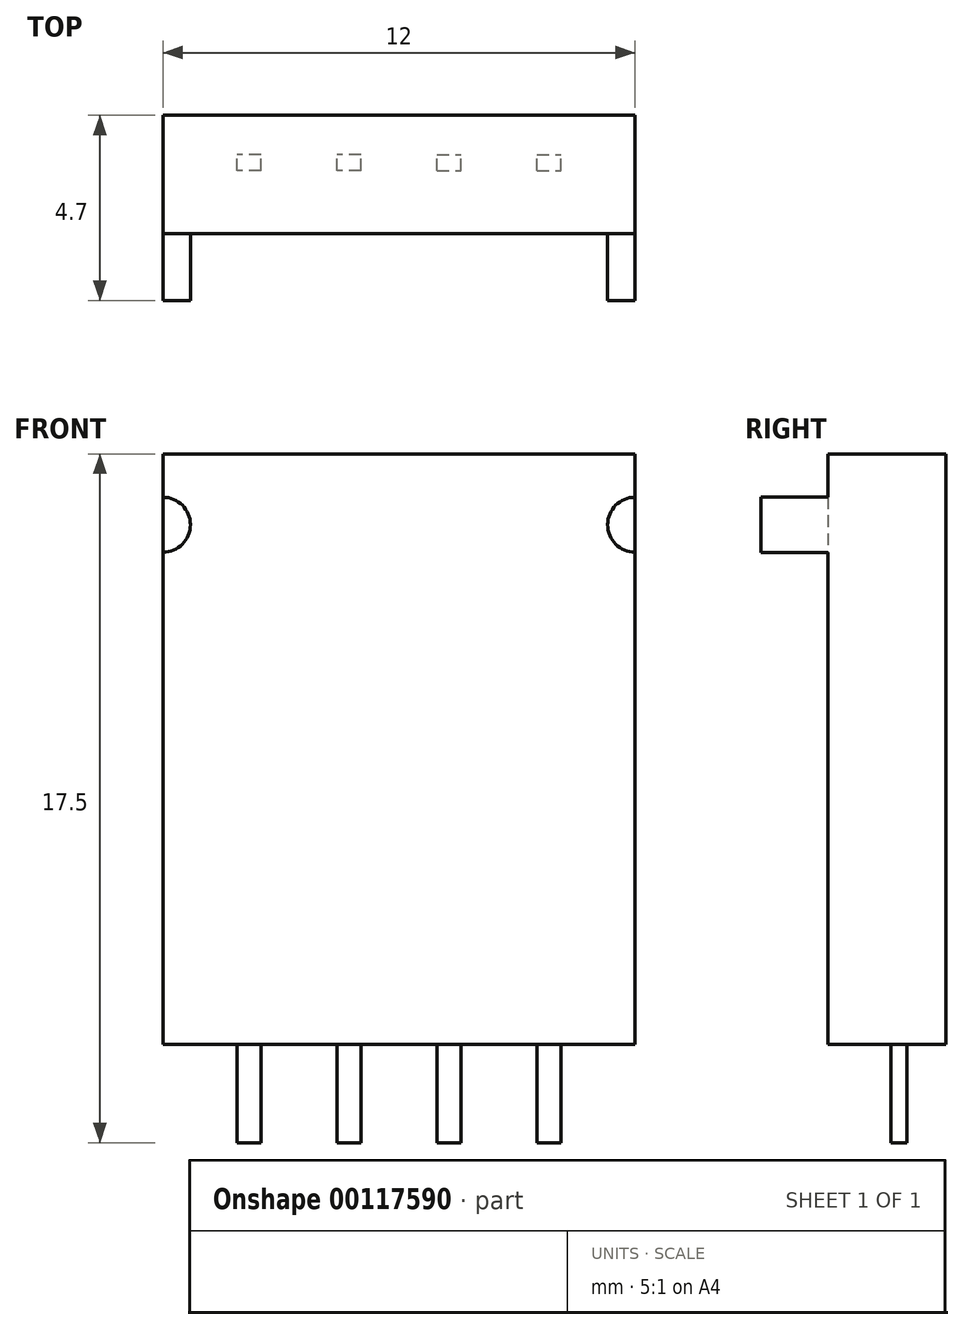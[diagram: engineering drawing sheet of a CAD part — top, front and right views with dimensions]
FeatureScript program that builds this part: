
annotation { "Feature Type Name" : "Feature", "Feature Type Description" : "" }
export const myFeature = defineFeature(function(context is Context, id is Id, definition is map)
    precondition{}
    {
        {
            var Q0;
            Q0=qCreatedBy(makeId("Front.planeOp"),FACE);
            var sketch = newSketch(context, id + "F0", { "sketchPlane" : qUnion([Q0])});
            skLineSegment(sketch, "E0.bottom", {"start": v(-6, 7.5) * mm, "end": v(6, 7.5) * mm});
            skLineSegment(sketch, "E0.top", {"start": v(-6, -7.5) * mm, "end": v(6, -7.5) * mm});
            skLineSegment(sketch, "E0.left", {"start": v(-6, 7.5) * mm, "end": v(-6, -7.5) * mm});
            skLineSegment(sketch, "E0.right", {"start": v(6, 7.5) * mm, "end": v(6, -7.5) * mm});
            skLineSegment(sketch, "E1", {"start": v(0, 7.5) * mm, "end": v(0, -7.5) * mm, "construction": true});
            skLineSegment(sketch, "E2", {"start": v(6, 0) * mm, "end": v(-6, 0) * mm, "construction": true});
            skSolve(sketch);
        }
        {
            var Q0;
            Q0=makeQuery(id+"F0.imprint","IMPRINT",FACE,{"disambiguationData":[TD([[makeQuery(id+"F0.imprint","IMPRINT",EDGE,{"derivedFrom":sQuery(id+"F0.wireOp",EDGE,"E0.bottom")}),-1.0]])]});
            extrude(context, id + "F1", {"entities" : qUnion([Q0]), "endBound" : BoundingType.SYMMETRIC, "depth" : 4.7 * mm});
        }
        {
            var Q0;
            Q0=makeQuery(id+"F1.opExtrude","CAP_FACE",FACE,{"disambiguationData":[OSD([sQuery(id+"F0.wireOp",EDGE,"E0.bottom"),sQuery(id+"F0.wireOp",EDGE,"E0.top"),sQuery(id+"F0.wireOp",EDGE,"E0.left"),sQuery(id+"F0.wireOp",EDGE,"E0.right")])],"isStart":false});
            var sketch = newSketch(context, id + "F2", { "sketchPlane" : qUnion([Q0])});
            skLineSegment(sketch, "E3", {"start": v(-4.2, -3.2) * mm, "end": v(-2.7, -3.2) * mm});
            skLineSegment(sketch, "E4", {"start": v(-4.2, -1.6) * mm, "end": v(-2.7, -1.6) * mm});
            skLineSegment(sketch, "E5", {"start": v(-4.2, -0.8) * mm, "end": v(-2.7, -0.8) * mm});
            skLineSegment(sketch, "E6", {"start": v(-4.2, 1.6) * mm, "end": v(-2.7, 1.6) * mm});
            skLineSegment(sketch, "E7", {"start": v(-4.2, 3.2) * mm, "end": v(-2.7, 3.2) * mm});
            skLineSegment(sketch, "E8", {"start": v(-4.2, 0.8) * mm, "end": v(-2.7, 0.8) * mm});
            skLineSegment(sketch, "E9", {"start": v(-4.2, -3.2) * mm, "end": v(-4.2, -1.6) * mm});
            skLineSegment(sketch, "E10", {"start": v(4.2, -3.2) * mm, "end": v(4.2, -1.6) * mm});
            skLineSegment(sketch, "E11", {"start": v(-2.7, 3.2) * mm, "end": v(-2.7, 1.6) * mm});
            skLineSegment(sketch, "E12", {"start": v(-1.9, 3.2) * mm, "end": v(-1.9, 1.6) * mm});
            skLineSegment(sketch, "E13", {"start": v(-0.4, 3.2) * mm, "end": v(-0.4, 1.6) * mm});
            skLineSegment(sketch, "E14", {"start": v(0.4, 3.2) * mm, "end": v(0.4, 1.6) * mm});
            skLineSegment(sketch, "E15", {"start": v(1.9, 3.2) * mm, "end": v(1.9, 1.6) * mm});
            skLineSegment(sketch, "E16", {"start": v(2.7, 3.2) * mm, "end": v(2.7, 1.6) * mm});
            skArc(sketch, "E17", {"start": v(6, -5) * mm, "mid": v(5.3, -5.7) * mm, "end": v(6, -6.4) * mm});
            skArc(sketch, "E18", {"start": v(-6, -6.4) * mm, "mid": v(-5.3, -5.7) * mm, "end": v(-6, -5) * mm});
            skArc(sketch, "E19", {"start": v(-0.7, 7.5) * mm, "mid": v(0, 6.8) * mm, "end": v(0.7, 7.5) * mm});
            skLineSegment(sketch, "E20", {"start": v(-6, -5.7) * mm, "end": v(6, -5.7) * mm, "construction": true});
            skArc(sketch, "E21.MirrorCS", {"start": v(6, 5) * mm, "mid": v(5.3, 5.7) * mm, "end": v(6, 6.4) * mm});
            skArc(sketch, "E22.MirrorCS", {"start": v(-6, 6.4) * mm, "mid": v(-5.3, 5.7) * mm, "end": v(-6, 5) * mm});
            skLineSegment(sketch, "E23.trimOffspring", {"start": v(-1.9, 3.2) * mm, "end": v(-0.4, 3.2) * mm});
            skLineSegment(sketch, "E24.trimOffspring", {"start": v(-1.9, 1.6) * mm, "end": v(-0.4, 1.6) * mm});
            skLineSegment(sketch, "E25.trimOffspring", {"start": v(-1.9, 0.8) * mm, "end": v(-0.4, 0.8) * mm});
            skLineSegment(sketch, "E26.trimOffspring", {"start": v(-2.7, 0.8) * mm, "end": v(-2.7, -0.8) * mm});
            skLineSegment(sketch, "E27.trimOffspring", {"start": v(-4.2, 1.6) * mm, "end": v(-4.2, 3.2) * mm});
            skLineSegment(sketch, "E28.trimOffspring", {"start": v(-4.2, -0.8) * mm, "end": v(-4.2, 0.8) * mm});
            skLineSegment(sketch, "E29.trimOffspring", {"start": v(-2.7, -1.6) * mm, "end": v(-2.7, -3.2) * mm});
            skLineSegment(sketch, "E30.trimOffspring", {"start": v(-1.9, -1.6) * mm, "end": v(-1.9, -3.2) * mm});
            skLineSegment(sketch, "E31.trimOffspring", {"start": v(-1.9, -0.8) * mm, "end": v(-0.4, -0.8) * mm});
            skLineSegment(sketch, "E32.trimOffspring", {"start": v(-1.9, -1.6) * mm, "end": v(-0.4, -1.6) * mm});
            skLineSegment(sketch, "E33.trimOffspring", {"start": v(-1.9, -3.2) * mm, "end": v(-0.4, -3.2) * mm});
            skLineSegment(sketch, "E34.trimOffspring", {"start": v(0.4, -3.2) * mm, "end": v(1.9, -3.2) * mm});
            skLineSegment(sketch, "E35.trimOffspring", {"start": v(0.4, -1.6) * mm, "end": v(1.9, -1.6) * mm});
            skLineSegment(sketch, "E36.trimOffspring", {"start": v(0.4, -0.8) * mm, "end": v(1.9, -0.8) * mm});
            skLineSegment(sketch, "E37.trimOffspring", {"start": v(0.4, 0.8) * mm, "end": v(1.9, 0.8) * mm});
            skLineSegment(sketch, "E38.trimOffspring", {"start": v(0.4, 1.6) * mm, "end": v(1.9, 1.6) * mm});
            skLineSegment(sketch, "E39.trimOffspring", {"start": v(0.4, 3.2) * mm, "end": v(1.9, 3.2) * mm});
            skLineSegment(sketch, "E40.trimOffspring", {"start": v(2.7, 3.2) * mm, "end": v(4.2, 3.2) * mm});
            skLineSegment(sketch, "E41.trimOffspring", {"start": v(2.7, 1.6) * mm, "end": v(4.2, 1.6) * mm});
            skLineSegment(sketch, "E42.trimOffspring", {"start": v(2.7, 0.8) * mm, "end": v(4.2, 0.8) * mm});
            skLineSegment(sketch, "E43.trimOffspring", {"start": v(2.7, -0.8) * mm, "end": v(4.2, -0.8) * mm});
            skLineSegment(sketch, "E44.trimOffspring", {"start": v(2.7, -1.6) * mm, "end": v(4.2, -1.6) * mm});
            skLineSegment(sketch, "E45.trimOffspring", {"start": v(2.7, -3.2) * mm, "end": v(4.2, -3.2) * mm});
            skLineSegment(sketch, "E46.trimOffspring", {"start": v(4.2, -0.8) * mm, "end": v(4.2, 0.8) * mm});
            skLineSegment(sketch, "E47.trimOffspring", {"start": v(2.7, -1.6) * mm, "end": v(2.7, -3.2) * mm});
            skLineSegment(sketch, "E48.trimOffspring", {"start": v(1.9, -1.6) * mm, "end": v(1.9, -3.2) * mm});
            skLineSegment(sketch, "E49.trimOffspring", {"start": v(0.4, -1.6) * mm, "end": v(0.4, -3.2) * mm});
            skLineSegment(sketch, "E50.trimOffspring", {"start": v(0.4, 0.8) * mm, "end": v(0.4, -0.8) * mm});
            skLineSegment(sketch, "E51.trimOffspring", {"start": v(1.9, 0.8) * mm, "end": v(1.9, -0.8) * mm});
            skLineSegment(sketch, "E52.trimOffspring", {"start": v(2.7, 0.8) * mm, "end": v(2.7, -0.8) * mm});
            skLineSegment(sketch, "E53.trimOffspring", {"start": v(4.2, 1.6) * mm, "end": v(4.2, 3.2) * mm});
            skLineSegment(sketch, "E54.trimOffspring", {"start": v(-1.9, 0.8) * mm, "end": v(-1.9, -0.8) * mm});
            skLineSegment(sketch, "E55.trimOffspring", {"start": v(-0.4, 0.8) * mm, "end": v(-0.4, -0.8) * mm});
            skLineSegment(sketch, "E56.trimOffspring", {"start": v(-0.4, -1.6) * mm, "end": v(-0.4, -3.2) * mm});
            skSolve(sketch);
        }
        {
            var Q0;
            {var subQ0=sQuery(id+"F2.wireOp",EDGE,"E22.MirrorCS");Q0=makeQuery(id+"F2.imprint","IMPRINT",FACE,{"disambiguationData":[TD([[makeQuery(id+"F2.imprint","IMPRINT",EDGE,{"derivedFrom":subQ0}),-1.0]])]});}
            var Q1;
            Q1=makeQuery(id+"F2.imprint","IMPRINT",FACE,{"disambiguationData":[TD([[makeQuery(id+"F2.imprint","IMPRINT",EDGE,{"derivedFrom":sQuery(id+"F2.wireOp",EDGE,"E6")}),1.0]])]});
            var Q2;
            Q2=makeQuery(id+"F2.imprint","IMPRINT",FACE,{"disambiguationData":[TD([[makeQuery(id+"F2.imprint","IMPRINT",EDGE,{"derivedFrom":sQuery(id+"F2.wireOp",EDGE,"E12")}),1.0]])]});
            var Q3;
            Q3=makeQuery(id+"F2.imprint","IMPRINT",FACE,{"disambiguationData":[TD([[makeQuery(id+"F2.imprint","IMPRINT",EDGE,{"derivedFrom":sQuery(id+"F2.wireOp",EDGE,"E14")}),1.0]])]});
            var Q4;
            Q4=makeQuery(id+"F2.imprint","IMPRINT",FACE,{"disambiguationData":[TD([[makeQuery(id+"F2.imprint","IMPRINT",EDGE,{"derivedFrom":sQuery(id+"F2.wireOp",EDGE,"E16")}),1.0]])]});
            var Q5;
            Q5=makeQuery(id+"F2.imprint","IMPRINT",FACE,{"disambiguationData":[TD([[makeQuery(id+"F2.imprint","IMPRINT",EDGE,{"derivedFrom":sQuery(id+"F2.wireOp",EDGE,"E42.trimOffspring")}),-1.0]])]});
            var Q6;
            Q6=makeQuery(id+"F2.imprint","IMPRINT",FACE,{"disambiguationData":[TD([[makeQuery(id+"F2.imprint","IMPRINT",EDGE,{"derivedFrom":sQuery(id+"F2.wireOp",EDGE,"E36.trimOffspring")}),1.0]])]});
            var Q7;
            Q7=makeQuery(id+"F2.imprint","IMPRINT",FACE,{"disambiguationData":[TD([[makeQuery(id+"F2.imprint","IMPRINT",EDGE,{"derivedFrom":sQuery(id+"F2.wireOp",EDGE,"E25.trimOffspring")}),-1.0]])]});
            var Q8;
            Q8=makeQuery(id+"F2.imprint","IMPRINT",FACE,{"disambiguationData":[TD([[makeQuery(id+"F2.imprint","IMPRINT",EDGE,{"derivedFrom":sQuery(id+"F2.wireOp",EDGE,"E5")}),1.0]])]});
            var Q9;
            Q9=makeQuery(id+"F2.imprint","IMPRINT",FACE,{"disambiguationData":[TD([[makeQuery(id+"F2.imprint","IMPRINT",EDGE,{"derivedFrom":sQuery(id+"F2.wireOp",EDGE,"E3")}),1.0]])]});
            var Q10;
            Q10=makeQuery(id+"F2.imprint","IMPRINT",FACE,{"disambiguationData":[TD([[makeQuery(id+"F2.imprint","IMPRINT",EDGE,{"derivedFrom":sQuery(id+"F2.wireOp",EDGE,"E30.trimOffspring")}),1.0]])]});
            var Q11;
            Q11=makeQuery(id+"F2.imprint","IMPRINT",FACE,{"disambiguationData":[TD([[makeQuery(id+"F2.imprint","IMPRINT",EDGE,{"derivedFrom":sQuery(id+"F2.wireOp",EDGE,"E34.trimOffspring")}),1.0]])]});
            var Q12;
            Q12=makeQuery(id+"F2.imprint","IMPRINT",FACE,{"disambiguationData":[TD([[makeQuery(id+"F2.imprint","IMPRINT",EDGE,{"derivedFrom":sQuery(id+"F2.wireOp",EDGE,"E10")}),1.0]])]});
            var Q13;
            {var subQ0=sQuery(id+"F2.wireOp",EDGE,"E17");Q13=makeQuery(id+"F2.imprint","IMPRINT",FACE,{"disambiguationData":[TD([[makeQuery(id+"F2.imprint","IMPRINT",EDGE,{"derivedFrom":subQ0}),1.0]])]});}
            var Q14;
            {var subQ0=sQuery(id+"F2.wireOp",EDGE,"E18");Q14=makeQuery(id+"F2.imprint","IMPRINT",FACE,{"disambiguationData":[TD([[makeQuery(id+"F2.imprint","IMPRINT",EDGE,{"derivedFrom":subQ0}),1.0]])]});}
            var Q15;
            {var subQ0=sQuery(id+"F2.wireOp",EDGE,"E21.MirrorCS");Q15=makeQuery(id+"F2.imprint","IMPRINT",FACE,{"disambiguationData":[TD([[makeQuery(id+"F2.imprint","IMPRINT",EDGE,{"derivedFrom":subQ0}),-1.0]])]});}
            var Q16;
            {var subQ0=sQuery(id+"F2.wireOp",EDGE,"E19");Q16=makeQuery(id+"F2.imprint","IMPRINT",FACE,{"disambiguationData":[TD([[makeQuery(id+"F2.imprint","IMPRINT",EDGE,{"derivedFrom":subQ0}),1.0]])]});}
            extrude(context, id + "F3", {"entities" : qUnion([Q0, Q1, Q2, Q3, Q4, Q5, Q6, Q7, Q8, Q9, Q10, Q11, Q12, Q13, Q14, Q15, Q16]), "operationType" : NewBodyOperationType.REMOVE, "oppositeDirection" : true, "depth" : 1.7 * mm});
        }
        {
            var Q0;
            Q0=makeQuery(id+"F1.opExtrude","SWEPT_FACE",FACE,{"disambiguationData":[OSD([sQuery(id+"F0.wireOp",EDGE,"E0.top")])]});
            var sketch = newSketch(context, id + "F4", { "sketchPlane" : qUnion([Q0])});
            skLineSegment(sketch, "E57.bottom", {"start": v(3.5, -0.95) * mm, "end": v(4.1, -0.95) * mm});
            skLineSegment(sketch, "E57.top", {"start": v(3.5, -1.35) * mm, "end": v(4.1, -1.35) * mm});
            skLineSegment(sketch, "E57.left", {"start": v(3.5, -0.95) * mm, "end": v(3.5, -1.35) * mm});
            skLineSegment(sketch, "E57.right", {"start": v(4.1, -0.95) * mm, "end": v(4.1, -1.35) * mm});
            skLineSegment(sketch, "E58.bottom", {"start": v(0.97, -0.95) * mm, "end": v(1.57, -0.95) * mm});
            skLineSegment(sketch, "E58.top", {"start": v(0.97, -1.35) * mm, "end": v(1.57, -1.35) * mm});
            skLineSegment(sketch, "E58.left", {"start": v(0.97, -0.95) * mm, "end": v(0.97, -1.35) * mm});
            skLineSegment(sketch, "E58.right", {"start": v(1.57, -0.95) * mm, "end": v(1.57, -1.35) * mm});
            skLineSegment(sketch, "E59.MirrorCS", {"start": v(-1.57, -0.95) * mm, "end": v(-1.57, -1.35) * mm});
            skLineSegment(sketch, "E60.MirrorCS", {"start": v(-3.5, -1.35) * mm, "end": v(-4.1, -1.35) * mm});
            skLineSegment(sketch, "E61.MirrorCS", {"start": v(-3.5, -0.95) * mm, "end": v(-4.1, -0.95) * mm});
            skLineSegment(sketch, "E62.MirrorCS", {"start": v(-3.5, -0.95) * mm, "end": v(-3.5, -1.35) * mm});
            skLineSegment(sketch, "E63.MirrorCS", {"start": v(-4.1, -0.95) * mm, "end": v(-4.1, -1.35) * mm});
            skLineSegment(sketch, "E64.MirrorCS", {"start": v(-0.97, -0.95) * mm, "end": v(-1.57, -0.95) * mm});
            skLineSegment(sketch, "E65.MirrorCS", {"start": v(-0.97, -0.95) * mm, "end": v(-0.97, -1.35) * mm});
            skLineSegment(sketch, "E66.MirrorCS", {"start": v(-0.97, -1.35) * mm, "end": v(-1.57, -1.35) * mm});
            skSolve(sketch);
        }
        {
            var Q0;
            Q0=makeQuery(id+"F4.imprint","IMPRINT",FACE,{"disambiguationData":[TD([[makeQuery(id+"F4.imprint","IMPRINT",EDGE,{"derivedFrom":sQuery(id+"F4.wireOp",EDGE,"E60.MirrorCS")}),-1.0]])]});
            var Q1;
            Q1=makeQuery(id+"F4.imprint","IMPRINT",FACE,{"disambiguationData":[TD([[makeQuery(id+"F4.imprint","IMPRINT",EDGE,{"derivedFrom":sQuery(id+"F4.wireOp",EDGE,"E59.MirrorCS")}),1.0]])]});
            var Q2;
            Q2=makeQuery(id+"F4.imprint","IMPRINT",FACE,{"disambiguationData":[TD([[makeQuery(id+"F4.imprint","IMPRINT",EDGE,{"derivedFrom":sQuery(id+"F4.wireOp",EDGE,"E58.bottom")}),-1.0]])]});
            var Q3;
            Q3=makeQuery(id+"F4.imprint","IMPRINT",FACE,{"disambiguationData":[TD([[makeQuery(id+"F4.imprint","IMPRINT",EDGE,{"derivedFrom":sQuery(id+"F4.wireOp",EDGE,"E57.bottom")}),-1.0]])]});
            extrude(context, id + "F5", {"entities" : qUnion([Q0, Q1, Q2, Q3]), "operationType" : NewBodyOperationType.ADD, "depth" : 2.5 * mm});
        }
    });
